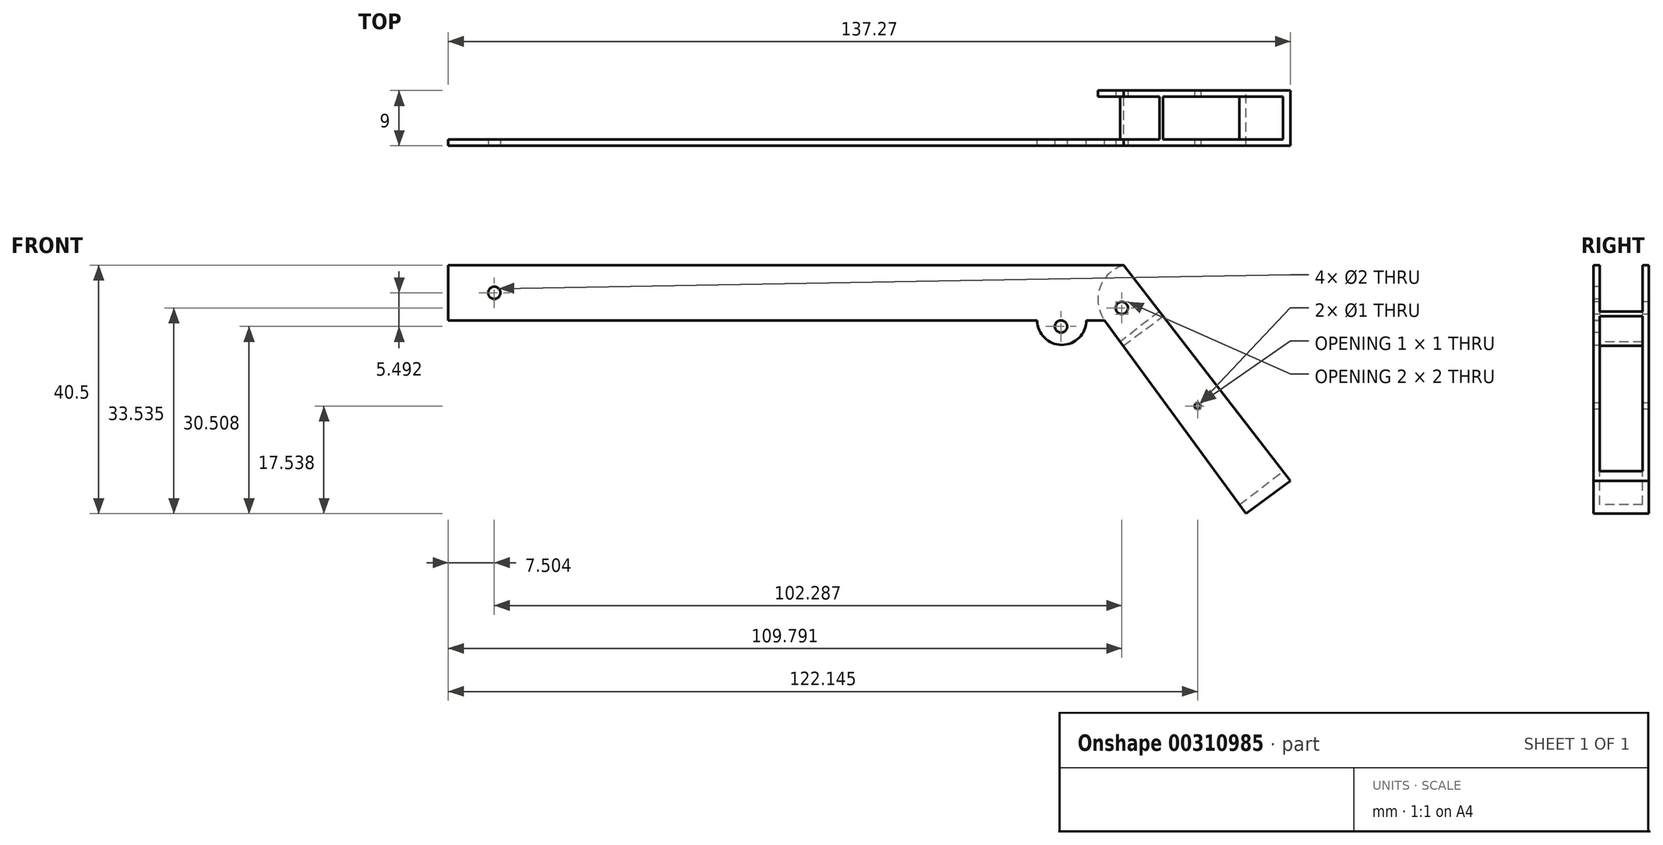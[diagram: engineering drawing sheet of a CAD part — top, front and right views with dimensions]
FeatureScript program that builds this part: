
annotation { "Feature Type Name" : "Feature", "Feature Type Description" : "" }
export const myFeature = defineFeature(function(context is Context, id is Id, definition is map)
    precondition{}
    {
        {
            var Q0;
            Q0=qCreatedBy(makeId("Front.planeOp"),FACE);
            var sketch = newSketch(context, id + "F0", { "sketchPlane" : qUnion([Q0])});
            skLineSegment(sketch, "E0", {"start": v(-64.99, 0) * mm, "end": v(42.01, 0) * mm});
            skLineSegment(sketch, "E1", {"start": v(42.01, 0) * mm, "end": v(65.01, -31.5) * mm});
            skLineSegment(sketch, "E2", {"start": v(-64.99, 0) * mm, "end": v(-64.99, 9) * mm});
            skLineSegment(sketch, "E3", {"start": v(-64.99, 9) * mm, "end": v(45.1, 9) * mm});
            skLineSegment(sketch, "E4", {"start": v(65.01, -31.5) * mm, "end": v(72.28, -26.19) * mm});
            skLineSegment(sketch, "E5", {"start": v(72.28, -26.19) * mm, "end": v(45.1, 9) * mm});
            skArc(sketch, "E6", {"start": v(31.01, 0) * mm, "mid": v(35.01, -4) * mm, "end": v(39.01, 0) * mm});
            skSolve(sketch);
        }
        {
            var Q0;
            Q0=makeQuery(id+"F0.imprint","IMPRINT",FACE,{"disambiguationData":[TD([[makeQuery(id+"F0.imprint","IMPRINT",EDGE,{"derivedFrom":sQuery(id+"F0.wireOp",EDGE,"E0")}),1.0]])]});
            var Q1;
            {var subQ0=sQuery(id+"F0.wireOp",EDGE,"eJEuzsmm-gpFT-pO60-1gQO-nRySk5jWklwk");Q1=makeQuery(id+"F0.imprint","IMPRINT",FACE,{"disambiguationData":[TD([[makeQuery(id+"F0.imprint","IMPRINT",EDGE,{"derivedFrom":subQ0}),1.0]])]});}
            var Q2;
            {var subQ0=sQuery(id+"F0.wireOp",EDGE,"E6");Q2=makeQuery(id+"F0.imprint","IMPRINT",FACE,{"disambiguationData":[TD([[makeQuery(id+"F0.imprint","IMPRINT",EDGE,{"derivedFrom":subQ0}),1.0]])]});}
            extrude(context, id + "F1", {"entities" : qUnion([Q0, Q1, Q2]), "depth" : 9 * mm});
        }
        {
            var Q0;
            Q0=makeQuery(id+"F1.opExtrude","CAP_FACE",FACE,{"disambiguationData":[OSD([sQuery(id+"F0.wireOp",EDGE,"E0"),sQuery(id+"F0.wireOp",EDGE,"E1"),sQuery(id+"F0.wireOp",EDGE,"E2"),sQuery(id+"F0.wireOp",EDGE,"E3"),sQuery(id+"F0.wireOp",EDGE,"E4"),sQuery(id+"F0.wireOp",EDGE,"E5")])],"isStart":true});
            var sketch = newSketch(context, id + "F2", { "sketchPlane" : qUnion([Q0])});
            skLineSegment(sketch, "E7", {"start": v(-42.01, 0) * mm, "end": v(-45.1, 9) * mm});
            skArc(sketch, "E8", {"start": v(-42.01, 0) * mm, "mid": v(-41.21, 5.3) * mm, "end": v(-45.1, 9) * mm});
            skSolve(sketch);
        }
        {
            var Q0;
            {var subQ1=makeQuery(id+"F1.opExtrude","CAP_EDGE",EDGE,{"disambiguationData":[OSD([sQuery(id+"F0.wireOp",EDGE,"E0")])],"isStart":true});Q0=makeQuery(id+"F2.imprint","IMPRINT",FACE,{"disambiguationData":[TD([[makeQuery(id+"F2.imprint","IMPRINT",EDGE,{"derivedFrom":subQ1}),-1.0]])]});}
            extrude(context, id + "F3", {"entities" : qUnion([Q0]), "operationType" : NewBodyOperationType.REMOVE, "oppositeDirection" : true, "depth" : 8 * mm});
        }
        {
            var Q0;
            Q0=makeQuery(id+"F1.opExtrude","SWEPT_FACE",FACE,{"disambiguationData":[OSD([sQuery(id+"F0.wireOp",EDGE,"E5")])]});
            var sketch = newSketch(context, id + "F4", { "sketchPlane" : qUnion([Q0])});
            skLineSegment(sketch, "E9.left", {"start": v(74.8, -62.9) * mm, "end": v(68.8, -62.9) * mm});
            skLineSegment(sketch, "E10.bottom", {"start": v(-1, -62.9) * mm, "end": v(-8, -62.9) * mm});
            skLineSegment(sketch, "E10.top", {"start": v(-1, -14.29) * mm, "end": v(-8, -14.29) * mm});
            skLineSegment(sketch, "E10.left", {"start": v(-1, -62.9) * mm, "end": v(-1, -14.29) * mm});
            skLineSegment(sketch, "E10.right", {"start": v(-8, -62.9) * mm, "end": v(-8, -14.29) * mm});
            skSolve(sketch);
        }
        {
            var Q0;
            {var subQ0=sQuery(id+"F4.wireOp",EDGE,"E10.bottom");Q0=makeQuery(id+"F4.imprint","IMPRINT",FACE,{"disambiguationData":[TD([[makeQuery(id+"F4.imprint","IMPRINT",EDGE,{"derivedFrom":subQ0}),-1.0]])]});}
            var Q1;
            {var subQ0=sQuery(id+"F4.wireOp",EDGE,"E10.top");Q1=makeQuery(id+"F4.imprint","IMPRINT",FACE,{"disambiguationData":[TD([[makeQuery(id+"F4.imprint","IMPRINT",EDGE,{"derivedFrom":subQ0}),1.0]])]});}
            extrude(context, id + "F5", {"entities" : qUnion([Q0, Q1]), "operationType" : NewBodyOperationType.REMOVE, "endBound" : BoundingType.THROUGH_ALL, "oppositeDirection" : true, "depth" : 25 * mm});
        }
        {
            var Q0;
            Q0=makeQuery(id+"F1.opExtrude","CAP_FACE",FACE,{"disambiguationData":[OSD([sQuery(id+"F0.wireOp",EDGE,"E0"),sQuery(id+"F0.wireOp",EDGE,"E1"),sQuery(id+"F0.wireOp",EDGE,"E2"),sQuery(id+"F0.wireOp",EDGE,"E3"),sQuery(id+"F0.wireOp",EDGE,"E4"),sQuery(id+"F0.wireOp",EDGE,"E5")])],"isStart":false});
            var sketch = newSketch(context, id + "F6", { "sketchPlane" : qUnion([Q0])});
            skLineSegment(sketch, "E11", {"start": v(51.55, 0.66) * mm, "end": v(45.01, -4.1) * mm});
            skLineSegment(sketch, "E12", {"start": v(45.01, -4.1) * mm, "end": v(44.55, -3.48) * mm});
            skLineSegment(sketch, "E13", {"start": v(44.55, -3.48) * mm, "end": v(50.94, 1.45) * mm});
            skLineSegment(sketch, "E14", {"start": v(50.94, 1.45) * mm, "end": v(51.55, 0.66) * mm});
            skSolve(sketch);
        }
        {
            var Q0;
            Q0=makeQuery(id+"F6.imprint","IMPRINT",FACE,{"disambiguationData":[TD([[makeQuery(id+"F6.imprint","IMPRINT",EDGE,{"derivedFrom":sQuery(id+"F6.wireOp",EDGE,"E11")}),-1.0]])]});
            extrude(context, id + "F7", {"entities" : qUnion([Q0]), "operationType" : NewBodyOperationType.ADD, "oppositeDirection" : true, "depth" : 9 * mm});
        }
        {
            var Q0;
            Q0=makeQuery(id+"F1.opExtrude","CAP_FACE",FACE,{"disambiguationData":[OSD([sQuery(id+"F0.wireOp",EDGE,"E0"),sQuery(id+"F0.wireOp",EDGE,"E1"),sQuery(id+"F0.wireOp",EDGE,"E2"),sQuery(id+"F0.wireOp",EDGE,"E3"),sQuery(id+"F0.wireOp",EDGE,"E4"),sQuery(id+"F0.wireOp",EDGE,"E5")])],"isStart":false});
            var sketch = newSketch(context, id + "F8", { "sketchPlane" : qUnion([Q0])});
            skCircle(sketch, "E15", {"center": v(57.15, -13.96) * mm, "radius": 0.5 * mm});
            skCircle(sketch, "E16", {"center": v(44.8, 2.04) * mm, "radius": 1 * mm});
            skCircle(sketch, "E17", {"center": v(-57.49, 4.5) * mm, "radius": 1 * mm});
            skPoint(sketch, "E17.centerSnap0", {"position": v(-64.99, 4.5) * mm});
            skSolve(sketch);
        }
        {
            var Q0;
            Q0=makeQuery(id+"F8.imprint","IMPRINT",FACE,{"disambiguationData":[TD([[makeQuery(id+"F8.imprint","IMPRINT",EDGE,{"derivedFrom":sQuery(id+"F8.wireOp",EDGE,"E16")}),1.0]])]});
            var Q1;
            Q1=makeQuery(id+"F8.imprint","IMPRINT",FACE,{"disambiguationData":[TD([[makeQuery(id+"F8.imprint","IMPRINT",EDGE,{"derivedFrom":sQuery(id+"F8.wireOp",EDGE,"E15")}),1.0]])]});
            var Q2;
            Q2=makeQuery(id+"F8.imprint","IMPRINT",FACE,{"disambiguationData":[TD([[makeQuery(id+"F8.imprint","IMPRINT",EDGE,{"derivedFrom":sQuery(id+"F8.wireOp",EDGE,"E17")}),1.0]])]});
            extrude(context, id + "F9", {"entities" : qUnion([Q0, Q1, Q2]), "operationType" : NewBodyOperationType.REMOVE, "endBound" : BoundingType.THROUGH_ALL, "oppositeDirection" : true, "depth" : 25 * mm});
        }
        {
            var Q0;
            Q0=makeQuery(id+"F1.opExtrude","CAP_FACE",FACE,{"disambiguationData":[OSD([sQuery(id+"F0.wireOp",EDGE,"E0"),sQuery(id+"F0.wireOp",EDGE,"E1"),sQuery(id+"F0.wireOp",EDGE,"E2"),sQuery(id+"F0.wireOp",EDGE,"E3"),sQuery(id+"F0.wireOp",EDGE,"E4"),sQuery(id+"F0.wireOp",EDGE,"E5"),sQuery(id+"F0.wireOp",EDGE,"eJEuzsmm-gpFT-pO60-1gQO-nRySk5jWklwk")])],"isStart":false});
            var sketch = newSketch(context, id + "F10", { "sketchPlane" : qUnion([Q0])});
            skCircle(sketch, "E18", {"center": v(-60.99, -1.47) * mm, "radius": 1 * mm});
            skCircle(sketch, "E19", {"center": v(34.89, -1) * mm, "radius": 1 * mm});
            skSolve(sketch);
        }
        {
            var Q0;
            Q0=makeQuery(id+"F10.imprint","IMPRINT",FACE,{"disambiguationData":[TD([[makeQuery(id+"F10.imprint","IMPRINT",EDGE,{"derivedFrom":sQuery(id+"F10.wireOp",EDGE,"E18")}),1.0]])]});
            var Q1;
            Q1=makeQuery(id+"F10.imprint","IMPRINT",FACE,{"disambiguationData":[TD([[makeQuery(id+"F10.imprint","IMPRINT",EDGE,{"derivedFrom":sQuery(id+"F10.wireOp",EDGE,"E19")}),1.0]])]});
            extrude(context, id + "F11", {"entities" : qUnion([Q0, Q1]), "operationType" : NewBodyOperationType.REMOVE, "endBound" : BoundingType.THROUGH_ALL, "oppositeDirection" : true, "depth" : 25 * mm});
        }
    });
